# Revit family: FJ2.100
name_source: partatom
category: Plumbing Fixtures
revit_build: Autodesk Revit Architecture 2012 (Build: 20110309_2315(x64)
units: mm (PartAtom-declared; Revit-internal decimal feet)

## types (1)
- FJ2.100
    Assembly Code = D2010
    CW Connection = Yes
    CWFU = 0
    Cost = 0 $
    Default Elevation = 0' - 0"
    Description = Exposed type. Back entry + flushpipe, connector, wall flange, seat buffer
    Flushpipe = FJT1.1
    HW Connection = No
    HWFU = 0
    Keynote = Built-in vacuum breaker. Prevents back syphonage.
    MAterial = Chrome - Polished
    Manufacturer = COBRA
    Model = FJ2.100
    Piston assembly = C-FJ8.10
    Pushbutton assembly = C-FJ8.20
    Range = Junior Flushmaster Flushvalves
    Rubber pan connector = C-FJV1.7
    Rubber seat buffer = C-FJV1.2
    Top cover = C-FJC1.2
    Type Comments = SANS 1240
    URL = http://www.cobra.co.za
    Vent Connection = No
    WFU = 0
    Waste Connection = No

## geometry (parser evidence)
native form markers: Blend x3
no freeform markers — native parametric forms only
